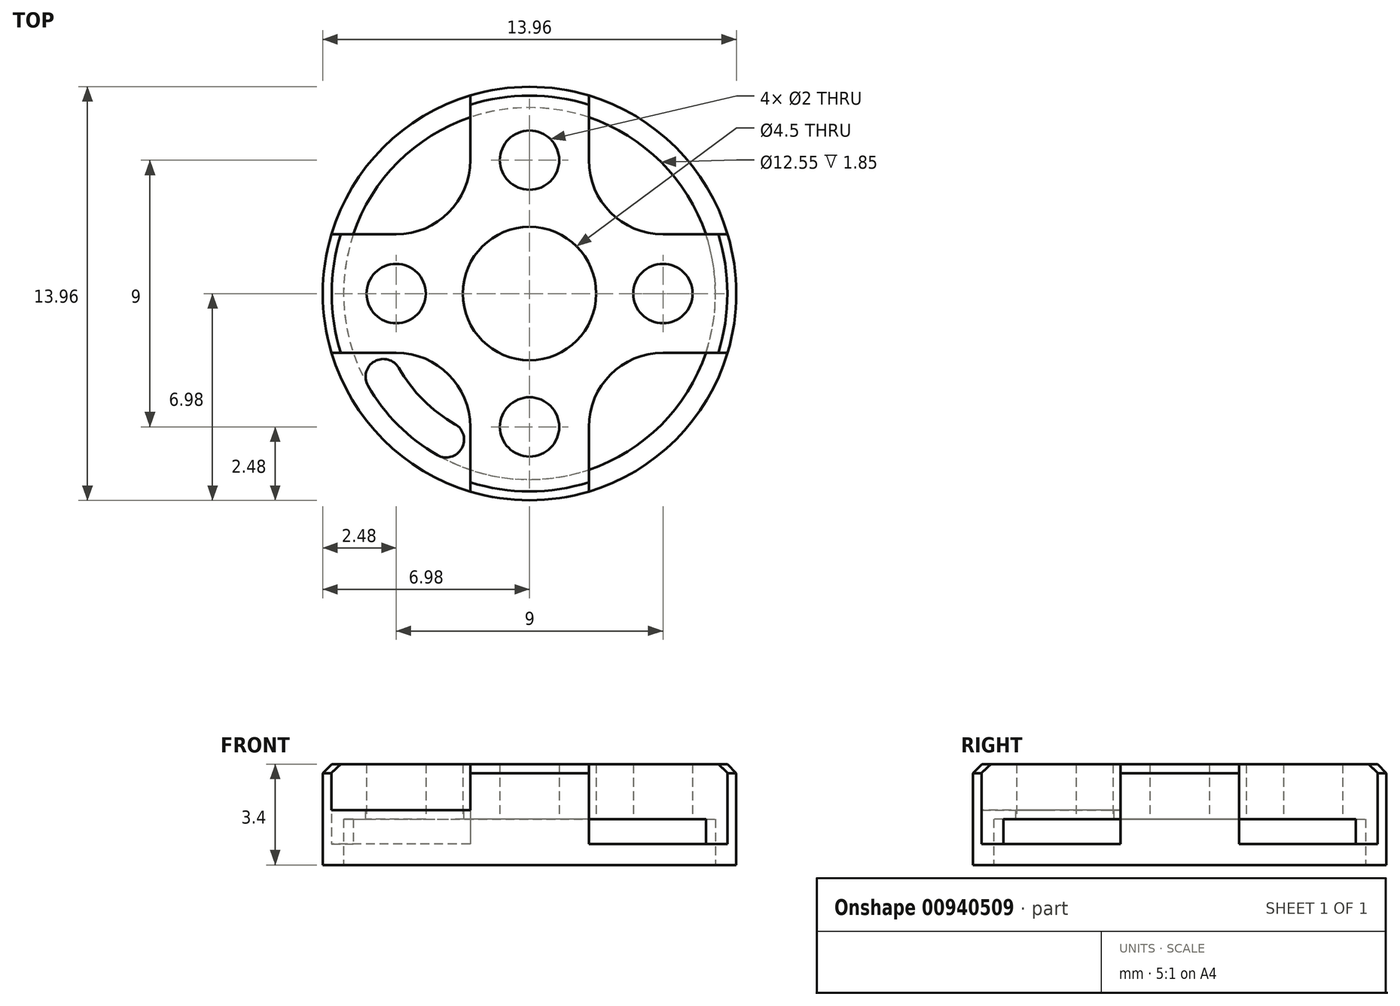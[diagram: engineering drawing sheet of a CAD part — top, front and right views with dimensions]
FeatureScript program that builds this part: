
annotation { "Feature Type Name" : "Feature", "Feature Type Description" : "" }
export const myFeature = defineFeature(function(context is Context, id is Id, definition is map)
    precondition{}
    {
        {
            var Q0;
            Q0=qCreatedBy(makeId("Top.planeOp"),FACE);
            var sketch = newSketch(context, id + "F0", { "sketchPlane" : qUnion([Q0])});
            skCircle(sketch, "E0", {"center": v(0, 0) * mm, "radius": 6.97 * mm});
            skCircle(sketch, "E1", {"center": v(0, 0) * mm, "radius": 2.25 * mm});
            skCircle(sketch, "E2", {"center": v(0, 4.5) * mm, "radius": 1 * mm});
            skLineSegment(sketch, "E3.top", {"start": v(-6.68, 2) * mm, "end": v(-2, 2) * mm});
            skLineSegment(sketch, "E3.right", {"start": v(-2, 6.68) * mm, "end": v(-2, 2) * mm});
            skCircle(sketch, "E4.1.0", {"center": v(-4.5, 0) * mm, "radius": 1 * mm});
            skLineSegment(sketch, "E4.1.1", {"start": v(-6.68, -2) * mm, "end": v(-2, -2) * mm});
            skLineSegment(sketch, "E4.1.2", {"start": v(-2, -6.68) * mm, "end": v(-2, -2) * mm});
            skCircle(sketch, "E4.2.0", {"center": v(0, -4.5) * mm, "radius": 1 * mm});
            skLineSegment(sketch, "E4.2.1", {"start": v(2, -6.68) * mm, "end": v(2, -2) * mm});
            skLineSegment(sketch, "E4.2.2", {"start": v(6.68, -2) * mm, "end": v(2, -2) * mm});
            skCircle(sketch, "E4.3.0", {"center": v(4.5, 0) * mm, "radius": 1 * mm});
            skLineSegment(sketch, "E4.3.1", {"start": v(6.68, 2) * mm, "end": v(2, 2) * mm});
            skLineSegment(sketch, "E4.3.2", {"start": v(2, 6.68) * mm, "end": v(2, 2) * mm});
            skCircle(sketch, "E5.0", {"center": v(0, 0) * mm, "radius": 6.27 * mm});
            skSolve(sketch);
        }
        {
            var Q0;
            {var subQ0=sQuery(id+"F0.wireOp",EDGE,"E3.right");var subQ1=sQuery(id+"F0.wireOp",EDGE,"E0");var subQ2=makeQuery(id+"F0.imprint","INTERSECT",VERTEX,{"derivedFrom":[subQ1,subQ0]});Q0=makeQuery(id+"F0.imprint","IMPRINT",FACE,{"disambiguationData":[TD([[makeQuery(id+"F0.imprint","IMPRINT",EDGE,{"disambiguationData":[TD([[subQ2,1.0]])],"derivedFrom":subQ1}),1.0]])]});}
            var Q1;
            Q1=makeQuery(id+"F0.imprint","IMPRINT",FACE,{"disambiguationData":[TD([[makeQuery(id+"F0.imprint","IMPRINT",EDGE,{"derivedFrom":sQuery(id+"F0.wireOp",EDGE,"E1")}),-1.0]])]});
            var Q2;
            {var subQ0=sQuery(id+"F0.wireOp",EDGE,"E4.2.2");var subQ1=sQuery(id+"F0.wireOp",EDGE,"E0");var subQ2=makeQuery(id+"F0.imprint","INTERSECT",VERTEX,{"derivedFrom":[subQ1,subQ0]});Q2=makeQuery(id+"F0.imprint","IMPRINT",FACE,{"disambiguationData":[TD([[makeQuery(id+"F0.imprint","IMPRINT",EDGE,{"disambiguationData":[TD([[subQ2,-1.0]])],"derivedFrom":subQ1}),1.0]])]});}
            var Q3;
            {var subQ0=sQuery(id+"F0.wireOp",EDGE,"E3.top");var subQ1=sQuery(id+"F0.wireOp",EDGE,"E0");var subQ2=makeQuery(id+"F0.imprint","INTERSECT",VERTEX,{"derivedFrom":[subQ1,subQ0]});Q3=makeQuery(id+"F0.imprint","IMPRINT",FACE,{"disambiguationData":[TD([[makeQuery(id+"F0.imprint","IMPRINT",EDGE,{"disambiguationData":[TD([[subQ2,-1.0]])],"derivedFrom":subQ1}),1.0]])]});}
            var Q4;
            {var subQ0=sQuery(id+"F0.wireOp",EDGE,"E4.1.2");var subQ1=sQuery(id+"F0.wireOp",EDGE,"E0");var subQ2=makeQuery(id+"F0.imprint","INTERSECT",VERTEX,{"derivedFrom":[subQ1,subQ0]});Q4=makeQuery(id+"F0.imprint","IMPRINT",FACE,{"disambiguationData":[TD([[makeQuery(id+"F0.imprint","IMPRINT",EDGE,{"disambiguationData":[TD([[subQ2,-1.0]])],"derivedFrom":subQ1}),1.0]])]});}
            extrude(context, id + "F1", {"entities" : qUnion([Q0, Q1, Q2, Q3, Q4]), "depth" : 3.4 * mm, "offsetDistance" : 25 * mm});
        }
        {
            var Q0;
            {var subQ0=sQuery(id+"F0.wireOp",EDGE,"E3.top");var subQ1=sQuery(id+"F0.wireOp",EDGE,"E0");var subQ2=makeQuery(id+"F0.imprint","INTERSECT",VERTEX,{"derivedFrom":[subQ1,subQ0]});Q0=makeQuery(id+"F0.imprint","IMPRINT",FACE,{"disambiguationData":[TD([[makeQuery(id+"F0.imprint","IMPRINT",EDGE,{"disambiguationData":[TD([[subQ2,1.0]])],"derivedFrom":subQ1}),1.0]])]});}
            var Q1;
            {var subQ0=sQuery(id+"F0.wireOp",EDGE,"E4.3.1");var subQ1=sQuery(id+"F0.wireOp",EDGE,"E0");var subQ2=makeQuery(id+"F0.imprint","INTERSECT",VERTEX,{"derivedFrom":[subQ1,subQ0]});Q1=makeQuery(id+"F0.imprint","IMPRINT",FACE,{"disambiguationData":[TD([[makeQuery(id+"F0.imprint","IMPRINT",EDGE,{"disambiguationData":[TD([[subQ2,-1.0]])],"derivedFrom":subQ1}),1.0]])]});}
            var Q2;
            {var subQ0=sQuery(id+"F0.wireOp",EDGE,"E4.2.1");var subQ1=sQuery(id+"F0.wireOp",EDGE,"E0");var subQ2=makeQuery(id+"F0.imprint","INTERSECT",VERTEX,{"derivedFrom":[subQ1,subQ0]});Q2=makeQuery(id+"F0.imprint","IMPRINT",FACE,{"disambiguationData":[TD([[makeQuery(id+"F0.imprint","IMPRINT",EDGE,{"disambiguationData":[TD([[subQ2,-1.0]])],"derivedFrom":subQ1}),1.0]])]});}
            extrude(context, id + "F2", {"entities" : qUnion([Q0, Q1, Q2]), "operationType" : NewBodyOperationType.ADD, "depth" : 0.7 * mm, "offsetDistance" : 25 * mm});
        }
        {
            var Q0;
            {var subQ0=sQuery(id+"F0.wireOp",EDGE,"E4.1.2");var subQ1=sQuery(id+"F0.wireOp",EDGE,"E4.1.1");var subQ2=makeQuery(id+"F0.imprint","INTERSECT",VERTEX,{"derivedFrom":[subQ1,subQ0]});Q0=makeQuery(id+"F0.imprint","IMPRINT",FACE,{"disambiguationData":[TD([[makeQuery(id+"F0.imprint","IMPRINT",EDGE,{"disambiguationData":[TD([[subQ2,1.0]])],"derivedFrom":subQ1}),-1.0]])]});}
            var Q1;
            {var subQ0=sQuery(id+"F0.wireOp",EDGE,"E4.1.1");var subQ1=sQuery(id+"F0.wireOp",EDGE,"E0");var subQ2=makeQuery(id+"F0.imprint","INTERSECT",VERTEX,{"derivedFrom":[subQ1,subQ0]});Q1=makeQuery(id+"F0.imprint","IMPRINT",FACE,{"disambiguationData":[TD([[makeQuery(id+"F0.imprint","IMPRINT",EDGE,{"disambiguationData":[TD([[subQ2,-1.0]])],"derivedFrom":subQ1}),1.0]])]});}
            var Q2;
            Q2=makeQuery(id+"F1.opExtrude","CAP_FACE",FACE,{"disambiguationData":[OSD([sQuery(id+"F0.wireOp",EDGE,"E0"),sQuery(id+"F0.wireOp",EDGE,"E1"),sQuery(id+"F0.wireOp",EDGE,"E2"),sQuery(id+"F0.wireOp",EDGE,"E3.top"),sQuery(id+"F0.wireOp",EDGE,"E3.right"),sQuery(id+"F0.wireOp",EDGE,"E4.1.0"),sQuery(id+"F0.wireOp",EDGE,"E4.1.1"),sQuery(id+"F0.wireOp",EDGE,"E4.1.2"),sQuery(id+"F0.wireOp",EDGE,"E4.2.0"),sQuery(id+"F0.wireOp",EDGE,"E4.2.1"),sQuery(id+"F0.wireOp",EDGE,"E4.2.2"),sQuery(id+"F0.wireOp",EDGE,"E4.3.0"),sQuery(id+"F0.wireOp",EDGE,"E4.3.1"),sQuery(id+"F0.wireOp",EDGE,"E4.3.2")])],"isStart":false});
            extrude(context, id + "F3", {"entities" : qUnion([Q0, Q1]), "operationType" : NewBodyOperationType.ADD, "endBound" : BoundingType.UP_TO_SURFACE, "depth" : 25 * mm, "endBoundEntityFace" : qUnion([Q2]), "hasOffset" : true, "offsetDistance" : 1.55 * mm});
        }
        {
            var Q0;
            Q0=makeQuery(id+"F0.imprint","IMPRINT",FACE,{"disambiguationData":[TD([[makeQuery(id+"F0.imprint","IMPRINT",EDGE,{"derivedFrom":sQuery(id+"F0.wireOp",EDGE,"E1")}),-1.0]])]});
            var Q1;
            {var subQ0=sQuery(id+"F0.wireOp",EDGE,"E4.1.2");var subQ1=sQuery(id+"F0.wireOp",EDGE,"E4.1.1");var subQ2=makeQuery(id+"F0.imprint","INTERSECT",VERTEX,{"derivedFrom":[subQ1,subQ0]});Q1=makeQuery(id+"F0.imprint","IMPRINT",FACE,{"disambiguationData":[TD([[makeQuery(id+"F0.imprint","IMPRINT",EDGE,{"disambiguationData":[TD([[subQ2,1.0]])],"derivedFrom":subQ1}),-1.0]])]});}
            var Q2;
            Q2=makeQuery(id+"F1.opExtrude","CAP_FACE",FACE,{"disambiguationData":[OSD([sQuery(id+"F0.wireOp",EDGE,"E0"),sQuery(id+"F0.wireOp",EDGE,"E1"),sQuery(id+"F0.wireOp",EDGE,"E2"),sQuery(id+"F0.wireOp",EDGE,"E3.top"),sQuery(id+"F0.wireOp",EDGE,"E3.right"),sQuery(id+"F0.wireOp",EDGE,"E4.1.0"),sQuery(id+"F0.wireOp",EDGE,"E4.1.1"),sQuery(id+"F0.wireOp",EDGE,"E4.1.2"),sQuery(id+"F0.wireOp",EDGE,"E4.2.0"),sQuery(id+"F0.wireOp",EDGE,"E4.2.1"),sQuery(id+"F0.wireOp",EDGE,"E4.2.2"),sQuery(id+"F0.wireOp",EDGE,"E4.3.0"),sQuery(id+"F0.wireOp",EDGE,"E4.3.1"),sQuery(id+"F0.wireOp",EDGE,"E4.3.2")])],"isStart":false});
            extrude(context, id + "F4", {"entities" : qUnion([Q0, Q1]), "operationType" : NewBodyOperationType.REMOVE, "endBound" : BoundingType.UP_TO_SURFACE, "depth" : 25 * mm, "endBoundEntityFace" : qUnion([Q2]), "hasOffset" : true, "offsetDistance" : 1.85 * mm});
        }
        {
            var Q0;
            Q0=makeQuery(id+"F1.opExtrude","SWEPT_EDGE",EDGE,{"disambiguationData":[OSD([sQuery(id+"F0.wireOp",EDGE,"E3.top"),sQuery(id+"F0.wireOp",EDGE,"E3.right")])]});
            var Q1;
            Q1=makeQuery(id+"F1.opExtrude","SWEPT_EDGE",EDGE,{"disambiguationData":[OSD([sQuery(id+"F0.wireOp",EDGE,"E4.1.1"),sQuery(id+"F0.wireOp",EDGE,"E4.1.2")])]});
            var Q2;
            Q2=makeQuery(id+"F1.opExtrude","SWEPT_EDGE",EDGE,{"disambiguationData":[OSD([sQuery(id+"F0.wireOp",EDGE,"E4.2.1"),sQuery(id+"F0.wireOp",EDGE,"E4.2.2")])]});
            var Q3;
            Q3=makeQuery(id+"F1.opExtrude","SWEPT_EDGE",EDGE,{"disambiguationData":[OSD([sQuery(id+"F0.wireOp",EDGE,"E4.3.1"),sQuery(id+"F0.wireOp",EDGE,"E4.3.2")])]});
            fillet(context, id + "F5", {"entities" : qUnion([Q0, Q1, Q2, Q3]), "radius" : 2.5 * mm, "tangentPropagation" : true, "allowEdgeOverflow" : false});
        }
        {
            var Q0;
            {var subQ0=sQuery(id+"F0.wireOp",EDGE,"E0");Q0=makeQuery(id+"F1.opExtrude","CAP_EDGE",EDGE,{"disambiguationData":[OSD([subQ0]),TDD([makeQuery(id+"F0.imprint","IMPRINT",EDGE,{"disambiguationData":[TD([[makeQuery(id+"F0.imprint","INTERSECT",VERTEX,{"derivedFrom":[subQ0,sQuery(id+"F0.wireOp",EDGE,"E4.1.2")]}),-1.0]])],"derivedFrom":subQ0})])],"isStart":false});}
            var Q1;
            {var subQ0=sQuery(id+"F0.wireOp",EDGE,"E0");Q1=makeQuery(id+"F1.opExtrude","CAP_EDGE",EDGE,{"disambiguationData":[OSD([subQ0]),TDD([makeQuery(id+"F0.imprint","IMPRINT",EDGE,{"disambiguationData":[TD([[makeQuery(id+"F0.imprint","INTERSECT",VERTEX,{"derivedFrom":[subQ0,sQuery(id+"F0.wireOp",EDGE,"E4.2.2")]}),-1.0]])],"derivedFrom":subQ0})])],"isStart":false});}
            var Q2;
            {var subQ0=sQuery(id+"F0.wireOp",EDGE,"E0");Q2=makeQuery(id+"F1.opExtrude","CAP_EDGE",EDGE,{"disambiguationData":[OSD([subQ0]),TDD([makeQuery(id+"F0.imprint","IMPRINT",EDGE,{"disambiguationData":[TD([[makeQuery(id+"F0.imprint","INTERSECT",VERTEX,{"derivedFrom":[subQ0,sQuery(id+"F0.wireOp",EDGE,"E3.right")]}),1.0]])],"derivedFrom":subQ0})])],"isStart":false});}
            var Q3;
            {var subQ0=sQuery(id+"F0.wireOp",EDGE,"E0");Q3=makeQuery(id+"F1.opExtrude","CAP_EDGE",EDGE,{"disambiguationData":[OSD([subQ0]),TDD([makeQuery(id+"F0.imprint","IMPRINT",EDGE,{"disambiguationData":[TD([[makeQuery(id+"F0.imprint","INTERSECT",VERTEX,{"derivedFrom":[subQ0,sQuery(id+"F0.wireOp",EDGE,"E3.top")]}),-1.0]])],"derivedFrom":subQ0})])],"isStart":false});}
            chamfer(context, id + "F6", {"entities" : qUnion([Q0, Q1, Q2, Q3]), "width" : 0.3 * mm, "tangentPropagation" : true});
        }
        {
            var Q0;
            Q0=makeQuery(id+"F3.opExtrude","CAP_FACE",FACE,{"disambiguationData":[OSD([sQuery(id+"F0.wireOp",EDGE,"E0"),sQuery(id+"F0.wireOp",EDGE,"E4.1.1"),sQuery(id+"F0.wireOp",EDGE,"E4.1.2")])],"isStart":false});
            var sketch = newSketch(context, id + "F7", { "sketchPlane" : qUnion([Q0])});
            skLineSegment(sketch, "E6", {"start": v(-2.73, -2.73) * mm, "end": v(-4.93, -4.93) * mm, "construction": true});
            skArc(sketch, "E7", {"start": v(-5.2, -2.27) * mm, "mid": v(-4.01, -4.01) * mm, "end": v(-2.27, -5.2) * mm, "construction": true});
            skCircle(sketch, "E8", {"center": v(-4.93, -2.8) * mm, "radius": 0.6 * mm});
            skCircle(sketch, "E9.MirrorC", {"center": v(-2.8, -4.93) * mm, "radius": 0.6 * mm});
            skArc(sketch, "E10", {"start": v(-2.51, -4.4) * mm, "mid": v(-3.59, -3.59) * mm, "end": v(-4.4, -2.51) * mm});
            skArc(sketch, "E11", {"start": v(-3.1, -5.45) * mm, "mid": v(-4.44, -4.44) * mm, "end": v(-5.45, -3.1) * mm});
            skSolve(sketch);
        }
        {
            var Q0;
            Q0 = qSketchRegion(id + "F7", true);
            extrude(context, id + "F8", {"entities" : qUnion([Q0]), "operationType" : NewBodyOperationType.REMOVE, "endBound" : BoundingType.THROUGH_ALL, "oppositeDirection" : true, "depth" : 25 * mm, "offsetDistance" : 25 * mm});
        }
    });
